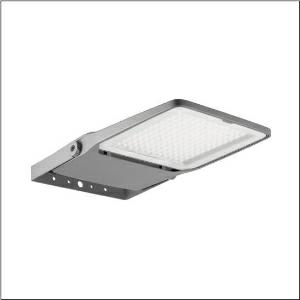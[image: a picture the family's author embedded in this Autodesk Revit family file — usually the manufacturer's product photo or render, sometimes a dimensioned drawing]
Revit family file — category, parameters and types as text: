
# Revit family: floodlight_fl_20_midi___rs17_5xa7682d1b2ac_3c54
name_source: partatom
category: Lighting Fixtures
units: mm (PartAtom-declared; Revit-internal decimal feet)

## family parameters
Cut with Voids When Loaded = No
Host = Face
Light Source = No
Part Type = Normal
Room Calculation Point = No
Round Connector Dimension = Use Diameter
Shared = No

## types (1)
- --- (1 x LED 3000K / CRI = 80 (unbekannt), 15350 lm, 3000K)
    Apparent Load = 142 VA
    CIE Flux Codes = 79 92 99 100 100
    Color Rendering = 80
    Color Temperature = 3000K
    Default Elevation = 1800 mm
    Description = Floodlight FL 20 midi, floodlight, primary light control with lens, of plastic, primary optical cover: protective disc, of toughened safety glass, transparent, light distribution: RS17, light emission: direct distribution, primary light characteristic: rotationally symmetric, installation type: surface-mounted, LED High Power LED, rated luminous flux: 15.350 lm, light colour: 830, colour temperature: 3000K, control gear: ECG Plus, control: flexible luminous flux parameterisation, time-dependent luminous flux control, digital communication interface, power reduction, overheat protection, electronic power reduction, with terminal, 5-pole, max. 2.5mm², mains connection: 220..240V, AC, 50/60Hz, rated input power: 142W, LED unit, of diecast aluminium, powder-coated, Siteco® metallic grey (DB 702S), length: 731 mm, width: 450 mm, height: 76mm, housing frame, of diecast aluminium, powder-coated, Siteco® metallic grey (DB 702S), wall fastening, of steel, powder-coated, Siteco® metallic grey (DB 702S), DALIprotection rating (complete): IP66, insulation class (complete): insulation class II (safety insulation), certification: CE, ENEC, VDE, protection symbol: D, permissible ambient temperature for indoor applications: -25..+40°C, permissible ambient temperature for outdoor applications: -40..+50°C, standard: DIN EN 12944, packaging unit: 1 piece

Light Distribution: RS17
    Height = 76 mm
    Lamp = 1 x LED 3000K / CRI >= 80 (unbekannt)
    Lamp Light Flux = 15350 lm
    Lamp count = 1
    Length = 731 mm
    Luminous efficacy = 108 lm/W
    Manufacturer = Siteco
    ModVariant = No
    Model = 5XA7682D1B2AC
    Number of Poles = 1
    OnlyDefault = Yes
    Power Factor = 1
    Product Name = Floodlight FL 20 midi | RS17
    Product group = floodlight | pylon top
    ProductGroupID = 6101
    Protection Class = Protection class II
    Protection Degree = IP 66
    RLX_Detail_Level = 1
    RlxData = <blob elided: 86509 chars, md5=01cd5e08>
    Socket = socket
    Standby Power = 0 W
    System Light Flux = 15350 lm
    System Power = 142 W
    Type Comments = factory setting: luminous flux: 100 % | dim-lin: 254 | 489 mA
    Type Image = l_1005944.jpg
    URL = http://relux.com
    VarID = @adj_142065
    Voltage = 0 V
    Weight = 0.00 kg
    Width = 450 mm

## geometry (parser evidence)
native form markers: Blend x4, Sweep x12
no freeform markers — native parametric forms only
